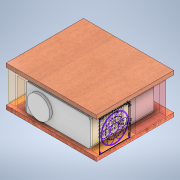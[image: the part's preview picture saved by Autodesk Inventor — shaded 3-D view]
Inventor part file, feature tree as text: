
AUTODESK INVENTOR PART (.ipt)
format: ipt  version: 2021.1 (Build 251245010, 245A)  size: 971,264 bytes
history: native  units: in
note: dims shown in document units (in); Inventor stores cm internally (conversion verified against a paired STEP export)
features: other x9, extrude x9, move_body x4, sketch x3, sheet_metal_op x1
ambient origin geometry x8: Origin, YZ Plane, XZ Plane, XY Plane, X Axis, Y Axis, Z Axis, Center Point
bodies: Body1 (feature_tree), Body2 (feature_tree), Body3 (feature_tree), Body4 (feature_tree), Body5 (feature_tree), Body6 (feature_tree)
feature tree (26):
  other  "bottom"
  sheet_metal_op  "face"
  extrude  "Extrusion9"  Depth=4.252in
  extrude  "Extrusion10"  Depth=4.1339in
  extrude  "Extrusion11"  Depth=4.7244in
  extrude  "Extrusion12"  Depth=0.9843in
  extrude  "Extrusion13"  Depth=4.7244in
  extrude  "Extrusion14"  Depth=0.315in
  extrude  "Extrusion15"  Depth=0.315in
  extrude  "Extrusion16"  Depth=0.1575in
  extrude  "Extrusion17"  Depth=13.7795in
  move_body  "Move Body1"
  move_body  "Move Body2"
  move_body  "Move Body3"
  move_body  "Move Body4"
  sketch  "Sketch6"  dims[d4=0.9843in d5=4.7244in d6=0.9843in d7=4.7244in d8=0.315in d9=0.315in d10=0.1575in d11=13.7795in d12=0.5906in d13=0.5906in d30=11.811in d31=0.0in d32=4.7244in d33=0.0in d34=4.1339in d35=0.0in d36=9.7638in d37=0.0in d38=0.5487in d39=0.0in d40=0.3612in d41=0.0in d42=11.811in d43=0.0in d45=0.315in d46=3.1496in d48=0.4724in d49=2.3622in d51=0.4724in d54=1.1265in d55=0.0in d57=3.1496in d59=2.3622in d60=0.315in d61=0.4724in d62=0.4724in d63=0.811in d64=0.0in d65=0.0in d66=0.0in d67=-0.3937in d68=0.0in d69=0.0in d70=-0.3937in d71=0.0in d72=0.0in d73=-0.3937in d74=0.0in d75=0.0in d76=-5.5118in d77=2.3622in d79=360.0deg d81=0.1575in d82=0.7874in d84=4.3307in d85=0.7874in d87=4.3307in]
  other  "fans"
  other  "TV-BOX"
  other  "Projector"
  other  "top"
  sketch  "Sketch4"  dims[d0=9.7638in d1=4.252in]
  sketch  "Sketch5"  dims[d2=1.1024in d3=4.1339in]
  other  "Composite1"
  other  "Composite2"
  other  "Srf1"
  other  "Srf2"
